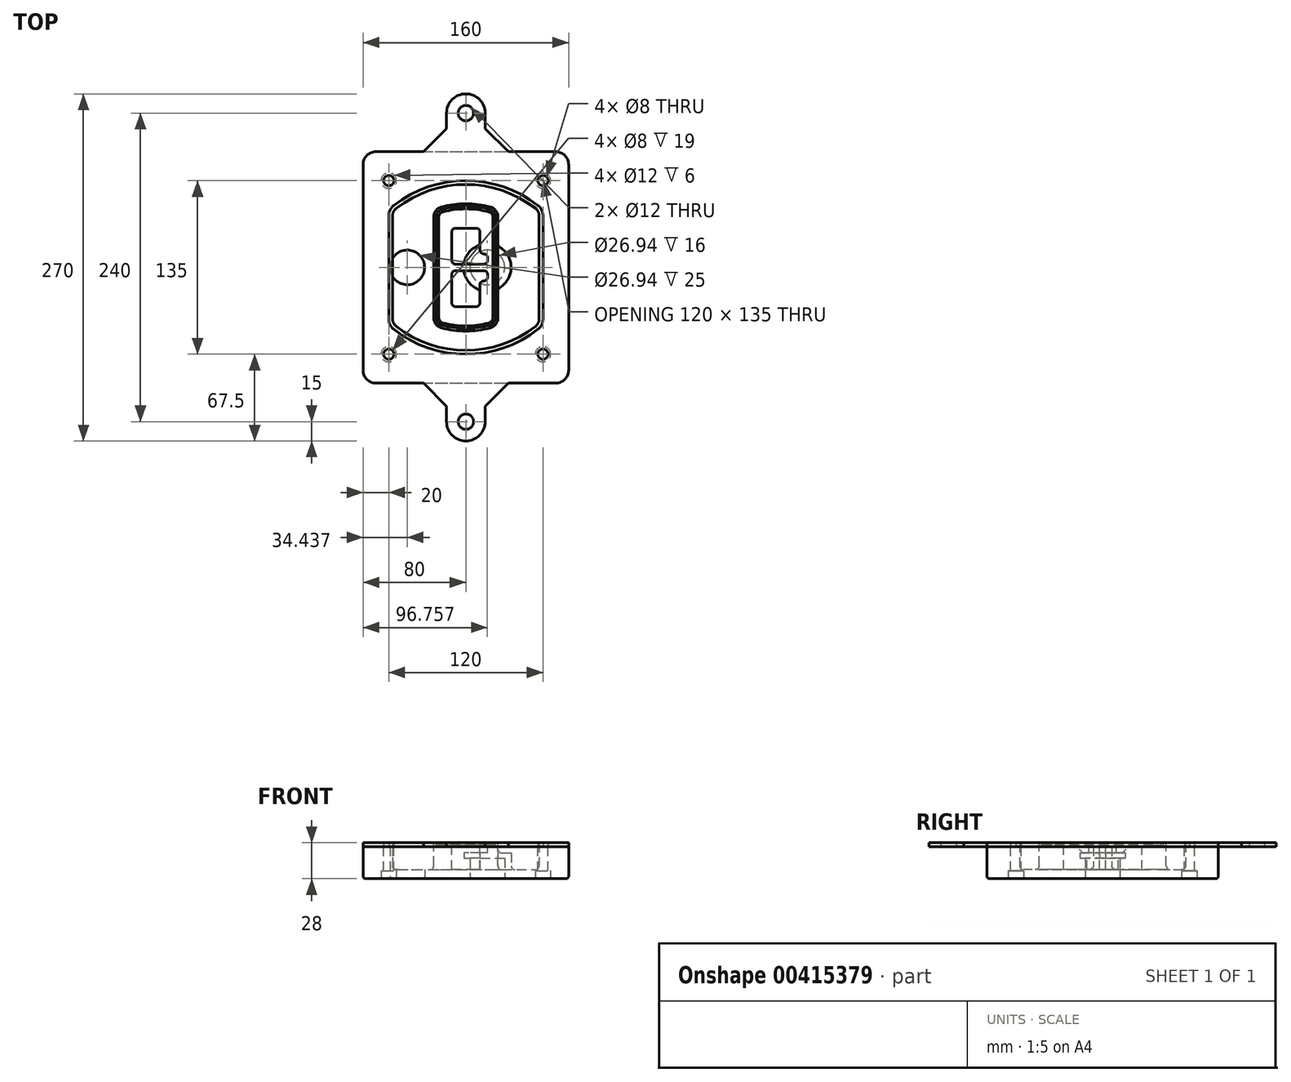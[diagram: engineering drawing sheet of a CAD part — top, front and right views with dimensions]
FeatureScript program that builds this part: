
annotation { "Feature Type Name" : "Feature", "Feature Type Description" : "" }
export const myFeature = defineFeature(function(context is Context, id is Id, definition is map)
    precondition{}
    {
        {
            var Q0;
            Q0=qCreatedBy(makeId("Top.planeOp"),FACE);
            var sketch = newSketch(context, id + "F0", { "sketchPlane" : qUnion([Q0])});
            skPoint(sketch, "E0.rect.middle", {"position": v(0, 0) * mm});
            skLineSegment(sketch, "E1.bottom", {"start": v(-70, -90) * mm, "end": v(70, -90) * mm});
            skLineSegment(sketch, "E1.top", {"start": v(-70, 90) * mm, "end": v(70, 90) * mm});
            skLineSegment(sketch, "E1.left", {"start": v(-80, -80) * mm, "end": v(-80, 80) * mm});
            skLineSegment(sketch, "E1.right", {"start": v(80, -80) * mm, "end": v(80, 80) * mm});
            skLineSegment(sketch, "E2", {"start": v(-80, 90) * mm, "end": v(80, -90) * mm, "construction": true});
            skLineSegment(sketch, "E3", {"start": v(80, 90) * mm, "end": v(-80, -90) * mm, "construction": true});
            skCircle(sketch, "E4", {"center": v(-60, 67.5) * mm, "radius": 4 * mm});
            skCircle(sketch, "E5", {"center": v(60, 67.5) * mm, "radius": 4 * mm});
            skCircle(sketch, "E6", {"center": v(60, -67.5) * mm, "radius": 4 * mm});
            skCircle(sketch, "E7", {"center": v(-60, -67.5) * mm, "radius": 4 * mm});
            skLineSegment(sketch, "E8", {"start": v(-60, 67.5) * mm, "end": v(60, 67.5) * mm, "construction": true});
            skLineSegment(sketch, "E9", {"start": v(60, 67.5) * mm, "end": v(60, -67.5) * mm, "construction": true});
            skLineSegment(sketch, "E10", {"start": v(60, -67.5) * mm, "end": v(-60, -67.5) * mm, "construction": true});
            skLineSegment(sketch, "E11", {"start": v(-60, -67.5) * mm, "end": v(-60, 67.5) * mm, "construction": true});
            skLineSegment(sketch, "E12", {"start": v(-60, 40.3) * mm, "end": v(-60, -40.3) * mm});
            skLineSegment(sketch, "E13", {"start": v(60, 40.3) * mm, "end": v(60, -40.3) * mm});
            skArc(sketch, "E14", {"start": v(56.15, 48.18) * mm, "mid": v(0, 67.5) * mm, "end": v(-56.15, 48.18) * mm});
            skArc(sketch, "E15", {"start": v(-56.15, -48.18) * mm, "mid": v(0, -67.5) * mm, "end": v(56.15, -48.18) * mm});
            skLineSegment(sketch, "E16", {"start": v(-60, 0) * mm, "end": v(60, 0) * mm, "construction": true});
            skPoint(sketch, "E17.visualSharp", {"position": v(-60, -45) * mm});
            skArc(sketch, "E17.filletArc", {"start": v(-60, -40.3) * mm, "mid": v(-58.99, -44.68) * mm, "end": v(-56.15, -48.18) * mm});
            skPoint(sketch, "E18.visualSharp", {"position": v(-60, 45) * mm});
            skArc(sketch, "E18.filletArc", {"start": v(-56.15, 48.18) * mm, "mid": v(-58.99, 44.68) * mm, "end": v(-60, 40.3) * mm});
            skPoint(sketch, "E19.visualSharp", {"position": v(60, 45) * mm});
            skArc(sketch, "E19.filletArc", {"start": v(60, 40.3) * mm, "mid": v(58.99, 44.68) * mm, "end": v(56.15, 48.18) * mm});
            skPoint(sketch, "E20.visualSharp", {"position": v(60, -45) * mm});
            skArc(sketch, "E20.filletArc", {"start": v(56.15, -48.18) * mm, "mid": v(58.99, -44.68) * mm, "end": v(60, -40.3) * mm});
            skPoint(sketch, "E21.visualSharp", {"position": v(-80, 90) * mm});
            skArc(sketch, "E21.filletArc", {"start": v(-70, 90) * mm, "mid": v(-77.07, 87.07) * mm, "end": v(-80, 80) * mm});
            skPoint(sketch, "E22.visualSharp", {"position": v(80, 90) * mm});
            skArc(sketch, "E22.filletArc", {"start": v(80, 80) * mm, "mid": v(77.07, 87.07) * mm, "end": v(70, 90) * mm});
            skPoint(sketch, "E23.visualSharp", {"position": v(80, -90) * mm});
            skArc(sketch, "E23.filletArc", {"start": v(70, -90) * mm, "mid": v(77.07, -87.07) * mm, "end": v(80, -80) * mm});
            skPoint(sketch, "E24.visualSharp", {"position": v(-80, -90) * mm});
            skArc(sketch, "E24.filletArc", {"start": v(-80, -80) * mm, "mid": v(-77.07, -87.07) * mm, "end": v(-70, -90) * mm});
            skArc(sketch, "E25.0", {"start": v(57, 40.3) * mm, "mid": v(56.3, 43.36) * mm, "end": v(54.3, 45.81) * mm});
            skLineSegment(sketch, "E25.1", {"start": v(57, 40.3) * mm, "end": v(57, -40.3) * mm});
            skArc(sketch, "E25.2", {"start": v(54.3, -45.81) * mm, "mid": v(56.3, -43.36) * mm, "end": v(57, -40.3) * mm});
            skArc(sketch, "E25.3", {"start": v(-54.3, -45.81) * mm, "mid": v(0, -64.5) * mm, "end": v(54.3, -45.81) * mm});
            skArc(sketch, "E25.4", {"start": v(-57, -40.3) * mm, "mid": v(-56.3, -43.36) * mm, "end": v(-54.3, -45.81) * mm});
            skArc(sketch, "E25.5", {"start": v(54.3, 45.81) * mm, "mid": v(0, 64.5) * mm, "end": v(-54.3, 45.81) * mm});
            skLineSegment(sketch, "E25.6", {"start": v(-57, 40.3) * mm, "end": v(-57, -40.3) * mm});
            skArc(sketch, "E25.7", {"start": v(-54.3, 45.81) * mm, "mid": v(-56.3, 43.36) * mm, "end": v(-57, 40.3) * mm});
            skArc(sketch, "E26.0", {"start": v(-58.62, 51.33) * mm, "mid": v(-62.58, 46.43) * mm, "end": v(-64, 40.3) * mm});
            skArc(sketch, "E26.1", {"start": v(58.62, 51.33) * mm, "mid": v(0, 71.5) * mm, "end": v(-58.62, 51.33) * mm});
            skArc(sketch, "E26.2", {"start": v(64, 40.3) * mm, "mid": v(62.58, 46.43) * mm, "end": v(58.62, 51.33) * mm});
            skLineSegment(sketch, "E26.3", {"start": v(64, 40.3) * mm, "end": v(64, -40.3) * mm});
            skArc(sketch, "E26.4", {"start": v(58.62, -51.33) * mm, "mid": v(62.58, -46.43) * mm, "end": v(64, -40.3) * mm});
            skLineSegment(sketch, "E26.5", {"start": v(-64, 40.3) * mm, "end": v(-64, -40.3) * mm});
            skArc(sketch, "E26.6", {"start": v(-58.62, -51.33) * mm, "mid": v(0, -71.5) * mm, "end": v(58.62, -51.33) * mm});
            skArc(sketch, "E26.7", {"start": v(-64, -40.3) * mm, "mid": v(-62.58, -46.43) * mm, "end": v(-58.62, -51.33) * mm});
            skSolve(sketch);
        }
        {
            var Q0;
            Q0=makeQuery(id+"F0.imprint","IMPRINT",FACE,{"disambiguationData":[TD([[makeQuery(id+"F0.imprint","IMPRINT",EDGE,{"derivedFrom":sQuery(id+"F0.wireOp",EDGE,"E1.bottom")}),1.0]])]});
            var Q1;
            Q1=makeQuery(id+"F0.imprint","IMPRINT",FACE,{"disambiguationData":[TD([[makeQuery(id+"F0.imprint","IMPRINT",EDGE,{"derivedFrom":sQuery(id+"F0.wireOp",EDGE,"E12")}),1.0]])]});
            var Q2;
            Q2=makeQuery(id+"F0.imprint","IMPRINT",FACE,{"disambiguationData":[TD([[makeQuery(id+"F0.imprint","IMPRINT",EDGE,{"derivedFrom":sQuery(id+"F0.wireOp",EDGE,"E25.0")}),1.0]])]});
            var Q3;
            Q3=makeQuery(id+"F0.imprint","IMPRINT",FACE,{"disambiguationData":[TD([[makeQuery(id+"F0.imprint","IMPRINT",EDGE,{"derivedFrom":sQuery(id+"F0.wireOp",EDGE,"E12")}),-1.0]])]});
            extrude(context, id + "F1", {"entities" : qUnion([Q0, Q1, Q2, Q3]), "oppositeDirection" : true, "depth" : 25 * mm});
        }
        {
            var Q0;
            Q0=makeQuery(id+"F0.imprint","IMPRINT",FACE,{"disambiguationData":[TD([[makeQuery(id+"F0.imprint","IMPRINT",EDGE,{"derivedFrom":sQuery(id+"F0.wireOp",EDGE,"E12")}),1.0]])]});
            extrude(context, id + "F2", {"entities" : qUnion([Q0]), "operationType" : NewBodyOperationType.ADD, "depth" : 3 * mm});
        }
        {
            var Q0;
            Q0=makeQuery(id+"F0.imprint","IMPRINT",FACE,{"disambiguationData":[TD([[makeQuery(id+"F0.imprint","IMPRINT",EDGE,{"derivedFrom":sQuery(id+"F0.wireOp",EDGE,"E25.0")}),1.0]])]});
            extrude(context, id + "F3", {"entities" : qUnion([Q0]), "operationType" : NewBodyOperationType.REMOVE, "oppositeDirection" : true, "depth" : 18 * mm});
        }
        {
            var Q0;
            Q0=makeQuery(id+"F2.opExtrude","CAP_FACE",FACE,{"disambiguationData":[OSD([sQuery(id+"F0.wireOp",EDGE,"E12"),sQuery(id+"F0.wireOp",EDGE,"E13"),sQuery(id+"F0.wireOp",EDGE,"E14"),sQuery(id+"F0.wireOp",EDGE,"E15"),sQuery(id+"F0.wireOp",EDGE,"E17.filletArc"),sQuery(id+"F0.wireOp",EDGE,"E18.filletArc"),sQuery(id+"F0.wireOp",EDGE,"E19.filletArc"),sQuery(id+"F0.wireOp",EDGE,"E20.filletArc"),sQuery(id+"F0.wireOp",EDGE,"E25.0"),sQuery(id+"F0.wireOp",EDGE,"E25.1"),sQuery(id+"F0.wireOp",EDGE,"E25.2"),sQuery(id+"F0.wireOp",EDGE,"E25.3"),sQuery(id+"F0.wireOp",EDGE,"E25.4"),sQuery(id+"F0.wireOp",EDGE,"E25.5"),sQuery(id+"F0.wireOp",EDGE,"E25.6"),sQuery(id+"F0.wireOp",EDGE,"E25.7")])],"isStart":false});
            var sketch = newSketch(context, id + "F4", { "sketchPlane" : qUnion([Q0])});
            skArc(sketch, "E27.0", {"start": v(-19.08, -46.97) * mm, "mid": v(0, -49.5) * mm, "end": v(19.08, -46.97) * mm});
            skArc(sketch, "E28.0", {"start": v(19.08, 46.97) * mm, "mid": v(0, 49.5) * mm, "end": v(-19.08, 46.97) * mm});
            skLineSegment(sketch, "E29", {"start": v(-25, 39.25) * mm, "end": v(-25, -39.25) * mm});
            skLineSegment(sketch, "E30", {"start": v(25, 39.25) * mm, "end": v(25, -39.25) * mm});
            skLineSegment(sketch, "E31", {"start": v(-25, 45.1) * mm, "end": v(25, 45.1) * mm, "construction": true});
            skLineSegment(sketch, "E32", {"start": v(-25, -45.1) * mm, "end": v(25, -45.1) * mm, "construction": true});
            skPoint(sketch, "E33.visualSharp", {"position": v(-25, 45.1) * mm});
            skArc(sketch, "E33.filletArc", {"start": v(-19.08, 46.97) * mm, "mid": v(-23.35, 44.11) * mm, "end": v(-25, 39.25) * mm});
            skPoint(sketch, "E34.visualSharp", {"position": v(25, 45.1) * mm});
            skArc(sketch, "E34.filletArc", {"start": v(25, 39.25) * mm, "mid": v(23.35, 44.11) * mm, "end": v(19.08, 46.97) * mm});
            skPoint(sketch, "E35.visualSharp", {"position": v(25, -45.1) * mm});
            skArc(sketch, "E35.filletArc", {"start": v(19.08, -46.97) * mm, "mid": v(23.35, -44.11) * mm, "end": v(25, -39.25) * mm});
            skPoint(sketch, "E36.visualSharp", {"position": v(-25, -45.1) * mm});
            skArc(sketch, "E36.filletArc", {"start": v(-25, -39.25) * mm, "mid": v(-23.35, -44.11) * mm, "end": v(-19.08, -46.97) * mm});
            skArc(sketch, "E37.0", {"start": v(54.3, 45.81) * mm, "mid": v(0, 64.5) * mm, "end": v(-54.3, 45.81) * mm});
            skArc(sketch, "E37.1", {"start": v(-54.3, 45.81) * mm, "mid": v(-56.3, 43.36) * mm, "end": v(-57, 40.3) * mm});
            skLineSegment(sketch, "E37.2", {"start": v(-57, 40.3) * mm, "end": v(-57, -40.3) * mm});
            skArc(sketch, "E37.3", {"start": v(-57, -40.3) * mm, "mid": v(-56.3, -43.36) * mm, "end": v(-54.3, -45.81) * mm});
            skArc(sketch, "E37.4", {"start": v(-54.3, -45.81) * mm, "mid": v(0, -64.5) * mm, "end": v(54.3, -45.81) * mm});
            skArc(sketch, "E37.5", {"start": v(54.3, -45.81) * mm, "mid": v(56.3, -43.36) * mm, "end": v(57, -40.3) * mm});
            skLineSegment(sketch, "E37.6", {"start": v(57, 40.3) * mm, "end": v(57, -40.3) * mm});
            skArc(sketch, "E37.7", {"start": v(57, 40.3) * mm, "mid": v(56.3, 43.36) * mm, "end": v(54.3, 45.81) * mm});
            skLineSegment(sketch, "E38.0", {"start": v(23, 39.25) * mm, "end": v(23, -39.25) * mm});
            skArc(sketch, "E38.1", {"start": v(18.56, -45.04) * mm, "mid": v(21.76, -42.9) * mm, "end": v(23, -39.25) * mm});
            skArc(sketch, "E38.2", {"start": v(-18.56, -45.04) * mm, "mid": v(0, -47.5) * mm, "end": v(18.56, -45.04) * mm});
            skArc(sketch, "E38.3", {"start": v(-23, -39.25) * mm, "mid": v(-21.76, -42.9) * mm, "end": v(-18.56, -45.04) * mm});
            skLineSegment(sketch, "E38.4", {"start": v(-23, 39.25) * mm, "end": v(-23, -39.25) * mm});
            skArc(sketch, "E38.5", {"start": v(23, 39.25) * mm, "mid": v(21.76, 42.9) * mm, "end": v(18.56, 45.04) * mm});
            skArc(sketch, "E38.6", {"start": v(-18.56, 45.04) * mm, "mid": v(-21.76, 42.9) * mm, "end": v(-23, 39.25) * mm});
            skArc(sketch, "E38.7", {"start": v(18.56, 45.04) * mm, "mid": v(0, 47.5) * mm, "end": v(-18.56, 45.04) * mm});
            skArc(sketch, "E39.0", {"start": v(21, 39.25) * mm, "mid": v(20.18, 41.68) * mm, "end": v(18.04, 43.1) * mm});
            skLineSegment(sketch, "E39.1", {"start": v(21, 39.25) * mm, "end": v(21, -39.25) * mm});
            skArc(sketch, "E39.2", {"start": v(18.04, -43.1) * mm, "mid": v(20.18, -41.68) * mm, "end": v(21, -39.25) * mm});
            skArc(sketch, "E39.3", {"start": v(-18.04, -43.1) * mm, "mid": v(0, -45.5) * mm, "end": v(18.04, -43.1) * mm});
            skArc(sketch, "E39.4", {"start": v(-21, -39.25) * mm, "mid": v(-20.18, -41.68) * mm, "end": v(-18.04, -43.1) * mm});
            skArc(sketch, "E39.5", {"start": v(18.04, 43.1) * mm, "mid": v(0, 45.5) * mm, "end": v(-18.04, 43.1) * mm});
            skLineSegment(sketch, "E39.6", {"start": v(-21, 39.25) * mm, "end": v(-21, -39.25) * mm});
            skArc(sketch, "E39.7", {"start": v(-18.04, 43.1) * mm, "mid": v(-20.18, 41.68) * mm, "end": v(-21, 39.25) * mm});
            skLineSegment(sketch, "E40", {"start": v(-25, 0) * mm, "end": v(25, 0) * mm, "construction": true});
            skLineSegment(sketch, "E41", {"start": v(-11, 5.5) * mm, "end": v(-11, 27.5) * mm});
            skLineSegment(sketch, "E42", {"start": v(-8, 30.5) * mm, "end": v(8, 30.5) * mm});
            skLineSegment(sketch, "E43", {"start": v(11, 27.5) * mm, "end": v(11, 13.5) * mm});
            skLineSegment(sketch, "E44", {"start": v(14, 10.5) * mm, "end": v(14, 10.5) * mm});
            skLineSegment(sketch, "E45", {"start": v(17, 7.5) * mm, "end": v(17, 5.5) * mm});
            skLineSegment(sketch, "E46", {"start": v(14, 2.5) * mm, "end": v(-8, 2.5) * mm});
            skPoint(sketch, "E47.visualSharp", {"position": v(-11, 30.5) * mm});
            skArc(sketch, "E47.filletArc", {"start": v(-8, 30.5) * mm, "mid": v(-10.12, 29.62) * mm, "end": v(-11, 27.5) * mm});
            skPoint(sketch, "E48.visualSharp", {"position": v(11, 30.5) * mm});
            skArc(sketch, "E48.filletArc", {"start": v(11, 27.5) * mm, "mid": v(10.12, 29.62) * mm, "end": v(8, 30.5) * mm});
            skPoint(sketch, "E49.visualSharp", {"position": v(11, 10.5) * mm});
            skArc(sketch, "E49.filletArc", {"start": v(11, 13.5) * mm, "mid": v(11.88, 11.38) * mm, "end": v(14, 10.5) * mm});
            skPoint(sketch, "E50.visualSharp", {"position": v(17, 10.5) * mm});
            skArc(sketch, "E50.filletArc", {"start": v(17, 7.5) * mm, "mid": v(16.12, 9.62) * mm, "end": v(14, 10.5) * mm});
            skPoint(sketch, "E51.visualSharp", {"position": v(17, 2.5) * mm});
            skArc(sketch, "E51.filletArc", {"start": v(14, 2.5) * mm, "mid": v(16.12, 3.38) * mm, "end": v(17, 5.5) * mm});
            skPoint(sketch, "E52.visualSharp", {"position": v(-11, 2.5) * mm});
            skArc(sketch, "E52.filletArc", {"start": v(-11, 5.5) * mm, "mid": v(-10.12, 3.38) * mm, "end": v(-8, 2.5) * mm});
            skLineSegment(sketch, "E53.0.MirrorCS", {"start": v(14, -2.5) * mm, "end": v(-8, -2.5) * mm});
            skArc(sketch, "E54.0.MirrorCS", {"start": v(-11, -5.5) * mm, "mid": v(-10.12, -3.38) * mm, "end": v(-8, -2.5) * mm});
            skLineSegment(sketch, "E55.0.MirrorCS", {"start": v(-11, -5.5) * mm, "end": v(-11, -27.5) * mm});
            skArc(sketch, "E56.0.MirrorCS", {"start": v(-8, -30.5) * mm, "mid": v(-10.12, -29.62) * mm, "end": v(-11, -27.5) * mm});
            skLineSegment(sketch, "E57.0.MirrorCS", {"start": v(-8, -30.5) * mm, "end": v(8, -30.5) * mm});
            skArc(sketch, "E58.0.MirrorCS", {"start": v(11, -27.5) * mm, "mid": v(10.12, -29.62) * mm, "end": v(8, -30.5) * mm});
            skLineSegment(sketch, "E59.0.MirrorCS", {"start": v(11, -27.5) * mm, "end": v(11, -13.5) * mm});
            skArc(sketch, "E60.0.MirrorCS", {"start": v(11, -13.5) * mm, "mid": v(11.88, -11.38) * mm, "end": v(14, -10.5) * mm});
            skArc(sketch, "E61.0.MirrorCS", {"start": v(17, -7.5) * mm, "mid": v(16.12, -9.62) * mm, "end": v(14, -10.5) * mm});
            skLineSegment(sketch, "E62.0.MirrorCS", {"start": v(17, -7.5) * mm, "end": v(17, -5.5) * mm});
            skArc(sketch, "E63.0.MirrorCS", {"start": v(14, -2.5) * mm, "mid": v(16.12, -3.38) * mm, "end": v(17, -5.5) * mm});
            skSolve(sketch);
        }
        {
            var Q0;
            Q0=makeQuery(id+"F4.imprint","IMPRINT",FACE,{"disambiguationData":[TD([[makeQuery(id+"F4.imprint","IMPRINT",EDGE,{"derivedFrom":sQuery(id+"F4.wireOp",EDGE,"E27.0")}),1.0]])]});
            var Q1;
            Q1=makeQuery(id+"F4.imprint","IMPRINT",FACE,{"disambiguationData":[TD([[makeQuery(id+"F4.imprint","IMPRINT",EDGE,{"derivedFrom":sQuery(id+"F4.wireOp",EDGE,"E38.0")}),-1.0]])]});
            var Q2;
            Q2=makeQuery(id+"F4.imprint","IMPRINT",FACE,{"disambiguationData":[TD([[makeQuery(id+"F4.imprint","IMPRINT",EDGE,{"derivedFrom":sQuery(id+"F4.wireOp",EDGE,"E39.0")}),1.0]])]});
            extrude(context, id + "F5", {"entities" : qUnion([Q0, Q1, Q2]), "operationType" : NewBodyOperationType.ADD, "endBound" : BoundingType.UP_TO_NEXT, "oppositeDirection" : true, "depth" : 25 * mm});
        }
        {
            var Q0;
            Q0=makeQuery(id+"F4.imprint","IMPRINT",FACE,{"disambiguationData":[TD([[makeQuery(id+"F4.imprint","IMPRINT",EDGE,{"derivedFrom":sQuery(id+"F4.wireOp",EDGE,"E38.0")}),-1.0]])]});
            extrude(context, id + "F6", {"entities" : qUnion([Q0]), "operationType" : NewBodyOperationType.REMOVE, "oppositeDirection" : true, "depth" : 2 * mm});
        }
        {
            var Q0;
            Q0=makeQuery(id+"F1.opExtrude","CAP_FACE",FACE,{"disambiguationData":[OSD([sQuery(id+"F0.wireOp",EDGE,"E1.bottom"),sQuery(id+"F0.wireOp",EDGE,"E1.top"),sQuery(id+"F0.wireOp",EDGE,"E1.left"),sQuery(id+"F0.wireOp",EDGE,"E1.right"),sQuery(id+"F0.wireOp",EDGE,"E4"),sQuery(id+"F0.wireOp",EDGE,"E5"),sQuery(id+"F0.wireOp",EDGE,"E6"),sQuery(id+"F0.wireOp",EDGE,"E7"),sQuery(id+"F0.wireOp",EDGE,"E21.filletArc"),sQuery(id+"F0.wireOp",EDGE,"E22.filletArc"),sQuery(id+"F0.wireOp",EDGE,"E23.filletArc"),sQuery(id+"F0.wireOp",EDGE,"E24.filletArc")])],"isStart":false});
            var sketch = newSketch(context, id + "F7", { "sketchPlane" : qUnion([Q0])});
            skCircle(sketch, "E64", {"center": v(16.76, 0) * mm, "radius": 13.47 * mm});
            skCircle(sketch, "E65", {"center": v(-45.56, 0) * mm, "radius": 13.47 * mm});
            skLineSegment(sketch, "E66", {"start": v(80, 0) * mm, "end": v(-80, 0) * mm});
            skCircle(sketch, "E67", {"center": v(16.76, 0) * mm, "radius": 18.47 * mm});
            skCircle(sketch, "E68", {"center": v(60, -67.5) * mm, "radius": 6 * mm});
            skCircle(sketch, "E69", {"center": v(-60, -67.5) * mm, "radius": 6 * mm});
            skCircle(sketch, "E70", {"center": v(-60, 67.5) * mm, "radius": 6 * mm});
            skCircle(sketch, "E71", {"center": v(60, 67.5) * mm, "radius": 6 * mm});
            skSolve(sketch);
        }
        {
            var Q0;
            {var subQ1=sQuery(id+"F7.wireOp",EDGE,"E66");var subQ4=sQuery(id+"F7.wireOp",EDGE,"E64");var subQ6=makeQuery(id+"F7.imprint","INTERSECT",VERTEX,{"disambiguationData":[OD(0.0)],"derivedFrom":[subQ4,subQ1]});Q0=makeQuery(id+"F7.imprint","IMPRINT",FACE,{"disambiguationData":[TD([[makeQuery(id+"F7.imprint","IMPRINT",EDGE,{"disambiguationData":[TD([[subQ6,-1.0]])],"derivedFrom":subQ4}),-1.0]])]});}
            var Q1;
            {var subQ0=sQuery(id+"F7.wireOp",EDGE,"E66");var subQ1=sQuery(id+"F7.wireOp",EDGE,"E64");var subQ3=makeQuery(id+"F7.imprint","INTERSECT",VERTEX,{"disambiguationData":[OD(0.0)],"derivedFrom":[subQ1,subQ0]});Q1=makeQuery(id+"F7.imprint","IMPRINT",FACE,{"disambiguationData":[TD([[makeQuery(id+"F7.imprint","IMPRINT",EDGE,{"disambiguationData":[TD([[subQ3,-1.0]])],"derivedFrom":subQ1}),1.0]])]});}
            var Q2;
            {var subQ0=sQuery(id+"F7.wireOp",EDGE,"E66");var subQ1=sQuery(id+"F7.wireOp",EDGE,"E64");var subQ3=makeQuery(id+"F7.imprint","INTERSECT",VERTEX,{"disambiguationData":[OD(0.0)],"derivedFrom":[subQ1,subQ0]});Q2=makeQuery(id+"F7.imprint","IMPRINT",FACE,{"disambiguationData":[TD([[makeQuery(id+"F7.imprint","IMPRINT",EDGE,{"disambiguationData":[TD([[subQ3,1.0]])],"derivedFrom":subQ1}),1.0]])]});}
            var Q3;
            {var subQ1=sQuery(id+"F7.wireOp",EDGE,"E66");var subQ4=sQuery(id+"F7.wireOp",EDGE,"E64");var subQ6=makeQuery(id+"F7.imprint","INTERSECT",VERTEX,{"disambiguationData":[OD(0.0)],"derivedFrom":[subQ4,subQ1]});Q3=makeQuery(id+"F7.imprint","IMPRINT",FACE,{"disambiguationData":[TD([[makeQuery(id+"F7.imprint","IMPRINT",EDGE,{"disambiguationData":[TD([[subQ6,1.0]])],"derivedFrom":subQ4}),-1.0]])]});}
            extrude(context, id + "F8", {"entities" : qUnion([Q0, Q1, Q2, Q3]), "operationType" : NewBodyOperationType.ADD, "oppositeDirection" : true, "depth" : 20 * mm});
        }
        {
            var Q0;
            {var subQ0=sQuery(id+"F7.wireOp",EDGE,"E66");var subQ1=sQuery(id+"F7.wireOp",EDGE,"E64");var subQ3=makeQuery(id+"F7.imprint","INTERSECT",VERTEX,{"disambiguationData":[OD(0.0)],"derivedFrom":[subQ1,subQ0]});Q0=makeQuery(id+"F7.imprint","IMPRINT",FACE,{"disambiguationData":[TD([[makeQuery(id+"F7.imprint","IMPRINT",EDGE,{"disambiguationData":[TD([[subQ3,-1.0]])],"derivedFrom":subQ1}),1.0]])]});}
            var Q1;
            {var subQ0=sQuery(id+"F7.wireOp",EDGE,"E66");var subQ1=sQuery(id+"F7.wireOp",EDGE,"E64");var subQ3=makeQuery(id+"F7.imprint","INTERSECT",VERTEX,{"disambiguationData":[OD(0.0)],"derivedFrom":[subQ1,subQ0]});Q1=makeQuery(id+"F7.imprint","IMPRINT",FACE,{"disambiguationData":[TD([[makeQuery(id+"F7.imprint","IMPRINT",EDGE,{"disambiguationData":[TD([[subQ3,1.0]])],"derivedFrom":subQ1}),1.0]])]});}
            extrude(context, id + "F9", {"entities" : qUnion([Q0, Q1]), "operationType" : NewBodyOperationType.REMOVE, "oppositeDirection" : true, "depth" : 16 * mm});
        }
        {
            var Q0;
            {var subQ0=sQuery(id+"F7.wireOp",EDGE,"E66");var subQ1=sQuery(id+"F7.wireOp",EDGE,"E65");var subQ3=makeQuery(id+"F7.imprint","INTERSECT",VERTEX,{"disambiguationData":[OD(0.0)],"derivedFrom":[subQ1,subQ0]});Q0=makeQuery(id+"F7.imprint","IMPRINT",FACE,{"disambiguationData":[TD([[makeQuery(id+"F7.imprint","IMPRINT",EDGE,{"disambiguationData":[TD([[subQ3,-1.0]])],"derivedFrom":subQ1}),1.0]])]});}
            var Q1;
            {var subQ0=sQuery(id+"F7.wireOp",EDGE,"E66");var subQ1=sQuery(id+"F7.wireOp",EDGE,"E65");var subQ3=makeQuery(id+"F7.imprint","INTERSECT",VERTEX,{"disambiguationData":[OD(0.0)],"derivedFrom":[subQ1,subQ0]});Q1=makeQuery(id+"F7.imprint","IMPRINT",FACE,{"disambiguationData":[TD([[makeQuery(id+"F7.imprint","IMPRINT",EDGE,{"disambiguationData":[TD([[subQ3,1.0]])],"derivedFrom":subQ1}),1.0]])]});}
            extrude(context, id + "F10", {"entities" : qUnion([Q0, Q1]), "operationType" : NewBodyOperationType.REMOVE, "oppositeDirection" : true, "depth" : 25 * mm});
        }
        {
            var Q0;
            Q0=makeQuery(id+"F7.imprint","IMPRINT",FACE,{"disambiguationData":[TD([[makeQuery(id+"F7.imprint","IMPRINT",EDGE,{"derivedFrom":sQuery(id+"F7.wireOp",EDGE,"E68")}),1.0]])]});
            var Q1;
            Q1=makeQuery(id+"F7.imprint","IMPRINT",FACE,{"disambiguationData":[TD([[makeQuery(id+"F7.imprint","IMPRINT",EDGE,{"derivedFrom":makeQuery(id+"F1.opExtrude","CAP_EDGE",EDGE,{"disambiguationData":[OSD([sQuery(id+"F0.wireOp",EDGE,"E5")])],"isStart":false})}),-1.0]])]});
            var Q2;
            Q2=makeQuery(id+"F7.imprint","IMPRINT",FACE,{"disambiguationData":[TD([[makeQuery(id+"F7.imprint","IMPRINT",EDGE,{"derivedFrom":sQuery(id+"F7.wireOp",EDGE,"E69")}),1.0]])]});
            var Q3;
            Q3=makeQuery(id+"F7.imprint","IMPRINT",FACE,{"disambiguationData":[TD([[makeQuery(id+"F7.imprint","IMPRINT",EDGE,{"derivedFrom":makeQuery(id+"F1.opExtrude","CAP_EDGE",EDGE,{"disambiguationData":[OSD([sQuery(id+"F0.wireOp",EDGE,"E4")])],"isStart":false})}),-1.0]])]});
            var Q4;
            Q4=makeQuery(id+"F7.imprint","IMPRINT",FACE,{"disambiguationData":[TD([[makeQuery(id+"F7.imprint","IMPRINT",EDGE,{"derivedFrom":sQuery(id+"F7.wireOp",EDGE,"E70")}),1.0]])]});
            var Q5;
            Q5=makeQuery(id+"F7.imprint","IMPRINT",FACE,{"disambiguationData":[TD([[makeQuery(id+"F7.imprint","IMPRINT",EDGE,{"derivedFrom":makeQuery(id+"F1.opExtrude","CAP_EDGE",EDGE,{"disambiguationData":[OSD([sQuery(id+"F0.wireOp",EDGE,"E7")])],"isStart":false})}),-1.0]])]});
            var Q6;
            Q6=makeQuery(id+"F7.imprint","IMPRINT",FACE,{"disambiguationData":[TD([[makeQuery(id+"F7.imprint","IMPRINT",EDGE,{"derivedFrom":sQuery(id+"F7.wireOp",EDGE,"E71")}),1.0]])]});
            var Q7;
            Q7=makeQuery(id+"F7.imprint","IMPRINT",FACE,{"disambiguationData":[TD([[makeQuery(id+"F7.imprint","IMPRINT",EDGE,{"derivedFrom":makeQuery(id+"F1.opExtrude","CAP_EDGE",EDGE,{"disambiguationData":[OSD([sQuery(id+"F0.wireOp",EDGE,"E6")])],"isStart":false})}),-1.0]])]});
            extrude(context, id + "F11", {"entities" : qUnion([Q0, Q1, Q2, Q3, Q4, Q5, Q6, Q7]), "operationType" : NewBodyOperationType.REMOVE, "oppositeDirection" : true, "depth" : 6 * mm});
        }
        {
            var Q0;
            Q0=makeQuery(id+"F9.boolean.opBoolean","COPY",FACE,{"derivedFrom":makeQuery(id+"F9.opExtrude","CAP_FACE",FACE,{"disambiguationData":[OSD([sQuery(id+"F7.wireOp",EDGE,"E64")])],"isStart":false})});
            var sketch = newSketch(context, id + "F12", { "sketchPlane" : qUnion([Q0])});
            skArc(sketch, "E72.0", {"start": v(11, 17.55) * mm, "mid": v(2.57, 11.82) * mm, "end": v(-1.54, 2.5) * mm});
            skArc(sketch, "E72.1", {"start": v(-1.54, -2.5) * mm, "mid": v(2.57, -11.82) * mm, "end": v(11, -17.55) * mm});
            skLineSegment(sketch, "E73", {"start": v(-1.54, -2.5) * mm, "end": v(14, -2.5) * mm});
            skLineSegment(sketch, "E74.0", {"start": v(14, 2.5) * mm, "end": v(-1.54, 2.5) * mm});
            skArc(sketch, "E74.1", {"start": v(14, 2.5) * mm, "mid": v(16.12, 3.38) * mm, "end": v(17, 5.5) * mm});
            skLineSegment(sketch, "E74.2", {"start": v(17, 7.5) * mm, "end": v(17, 5.5) * mm});
            skArc(sketch, "E74.3", {"start": v(17, 7.5) * mm, "mid": v(16.12, 9.62) * mm, "end": v(14, 10.5) * mm});
            skArc(sketch, "E74.4", {"start": v(11, 13.5) * mm, "mid": v(11.88, 11.38) * mm, "end": v(14, 10.5) * mm});
            skLineSegment(sketch, "E74.5", {"start": v(11, 17.55) * mm, "end": v(11, 13.5) * mm});
            skLineSegment(sketch, "E74.7", {"start": v(14, -2.5) * mm, "end": v(-1.54, -2.5) * mm});
            skArc(sketch, "E74.8", {"start": v(14, -2.5) * mm, "mid": v(16.12, -3.38) * mm, "end": v(17, -5.5) * mm});
            skLineSegment(sketch, "E74.9", {"start": v(17, -7.5) * mm, "end": v(17, -5.5) * mm});
            skArc(sketch, "E74.10", {"start": v(17, -7.5) * mm, "mid": v(16.12, -9.62) * mm, "end": v(14, -10.5) * mm});
            skArc(sketch, "E74.11", {"start": v(11, -13.5) * mm, "mid": v(11.88, -11.38) * mm, "end": v(14, -10.5) * mm});
            skLineSegment(sketch, "E74.12", {"start": v(11, -17.55) * mm, "end": v(11, -13.5) * mm});
            skPoint(sketch, "E75.orphan", {"position": v(11, -27.5) * mm});
            skPoint(sketch, "E76.orphan", {"position": v(-8, -2.5) * mm});
            skPoint(sketch, "E77.orphan", {"position": v(-8, 2.5) * mm});
            skPoint(sketch, "E78.orphan", {"position": v(11, 27.5) * mm});
            skSolve(sketch);
        }
        {
            var Q0;
            {var subQ7=sQuery(id+"F12.wireOp",EDGE,"E72.0");var subQ14=sQuery(id+"F12.wireOp",EDGE,"E72.1");var subQ16=sQuery(id+"F12.wireOp",EDGE,"E74.1");var subQ18=sQuery(id+"F12.wireOp",EDGE,"E74.8");Q0=qUnion([makeQuery(id+"F12.imprint","IMPRINT",FACE,{"disambiguationData":[TD([[makeQuery(id+"F12.imprint","IMPRINT",EDGE,{"derivedFrom":subQ7}),1.0]])]}),makeQuery(id+"F12.imprint","IMPRINT",FACE,{"disambiguationData":[TD([[makeQuery(id+"F12.imprint","IMPRINT",EDGE,{"derivedFrom":subQ14}),1.0]])]}),makeQuery(id+"F12.imprint","IMPRINT",FACE,{"disambiguationData":[TD([[makeQuery(id+"F12.imprint","IMPRINT",EDGE,{"derivedFrom":subQ16}),1.0]])]}),makeQuery(id+"F12.imprint","IMPRINT",FACE,{"disambiguationData":[TD([[makeQuery(id+"F12.imprint","IMPRINT",EDGE,{"derivedFrom":subQ18}),-1.0]])]})]);}
            var Q1;
            Q1=makeQuery(id+"F5.boolean.opBoolean","SPLIT",FACE,{"disambiguationData":[TD([makeQuery(id+"F5.opExtrude","SWEPT_FACE",FACE,{"disambiguationData":[OSD([sQuery(id+"F4.wireOp",EDGE,"E41")])]})])],"derivedFrom":makeQuery(id+"F3.boolean.opBoolean","COPY",FACE,{"derivedFrom":makeQuery(id+"F3.opExtrude","CAP_FACE",FACE,{"disambiguationData":[OSD([sQuery(id+"F0.wireOp",EDGE,"E25.0"),sQuery(id+"F0.wireOp",EDGE,"E25.1"),sQuery(id+"F0.wireOp",EDGE,"E25.2"),sQuery(id+"F0.wireOp",EDGE,"E25.3"),sQuery(id+"F0.wireOp",EDGE,"E25.4"),sQuery(id+"F0.wireOp",EDGE,"E25.5"),sQuery(id+"F0.wireOp",EDGE,"E25.6"),sQuery(id+"F0.wireOp",EDGE,"E25.7")])],"isStart":false})})});
            extrude(context, id + "F13", {"entities" : qUnion([Q0]), "operationType" : NewBodyOperationType.REMOVE, "endBound" : BoundingType.UP_TO_SURFACE, "endBoundEntityFace" : qUnion([Q1]), "depth" : 25 * mm});
        }
        {
            var Q0;
            Q0=makeQuery(id+"F3.boolean.opBoolean","COPY",EDGE,{"derivedFrom":makeQuery(id+"F3.opExtrude","CAP_EDGE",EDGE,{"disambiguationData":[OSD([sQuery(id+"F0.wireOp",EDGE,"E25.6")])],"isStart":false})});
            var Q1;
            Q1=makeQuery(id+"F8.boolean.opBoolean","INTERSECT",EDGE,{"derivedFrom":[makeQuery(id+"F5.opExtrude","SWEPT_FACE",FACE,{"disambiguationData":[OSD([sQuery(id+"F4.wireOp",EDGE,"E30")])]}),makeQuery(id+"F8.opExtrude","CAP_FACE",FACE,{"disambiguationData":[OSD([sQuery(id+"F7.wireOp",EDGE,"E67")])],"isStart":false})]});
            var Q2;
            Q2=makeQuery(id+"F8.boolean.opBoolean","INTERSECT",EDGE,{"disambiguationData":[OD(1.0)],"derivedFrom":[makeQuery(id+"F5.opExtrude","SWEPT_FACE",FACE,{"disambiguationData":[OSD([sQuery(id+"F4.wireOp",EDGE,"E30")])]}),makeQuery(id+"F8.opExtrude","SWEPT_FACE",FACE,{"disambiguationData":[OSD([sQuery(id+"F7.wireOp",EDGE,"E67")])]})]});
            var Q3;
            {var subQ0=sQuery(id+"F4.wireOp",EDGE,"E30");Q3=makeQuery(id+"F8.boolean.opBoolean","SPLIT",EDGE,{"disambiguationData":[TD([makeQuery(id+"F5.opExtrude","SWEPT_FACE",FACE,{"disambiguationData":[OSD([sQuery(id+"F4.wireOp",EDGE,"E35.filletArc")])]})])],"derivedFrom":makeQuery(id+"F5.opExtrude","CAP_EDGE",EDGE,{"disambiguationData":[OSD([subQ0])],"isStart":false})});}
            var Q4;
            {var subQ0=sQuery(id+"F0.wireOp",EDGE,"E25.7");var subQ1=sQuery(id+"F0.wireOp",EDGE,"E25.1");var subQ2=sQuery(id+"F0.wireOp",EDGE,"E25.6");var subQ3=sQuery(id+"F0.wireOp",EDGE,"E25.5");var subQ4=sQuery(id+"F0.wireOp",EDGE,"E25.4");var subQ5=sQuery(id+"F0.wireOp",EDGE,"E25.0");var subQ6=sQuery(id+"F0.wireOp",EDGE,"E25.2");var subQ7=sQuery(id+"F0.wireOp",EDGE,"E25.3");Q4=makeQuery(id+"F8.boolean.opBoolean","INTERSECT",EDGE,{"derivedFrom":[makeQuery(id+"F5.boolean.opBoolean","SPLIT",FACE,{"disambiguationData":[TD([makeQuery(id+"F2.opExtrude","SWEPT_FACE",FACE,{"disambiguationData":[OSD([subQ5])]})])],"derivedFrom":makeQuery(id+"F3.boolean.opBoolean","COPY",FACE,{"derivedFrom":makeQuery(id+"F3.opExtrude","CAP_FACE",FACE,{"disambiguationData":[OSD([subQ5,subQ1,subQ6,subQ7,subQ4,subQ3,subQ2,subQ0])],"isStart":false})})}),makeQuery(id+"F8.opExtrude","SWEPT_FACE",FACE,{"disambiguationData":[OSD([sQuery(id+"F7.wireOp",EDGE,"E67")])]})]});}
            var Q5;
            Q5=makeQuery(id+"F8.boolean.opBoolean","INTERSECT",EDGE,{"disambiguationData":[OD(0.0)],"derivedFrom":[makeQuery(id+"F5.opExtrude","SWEPT_FACE",FACE,{"disambiguationData":[OSD([sQuery(id+"F4.wireOp",EDGE,"E30")])]}),makeQuery(id+"F8.opExtrude","SWEPT_FACE",FACE,{"disambiguationData":[OSD([sQuery(id+"F7.wireOp",EDGE,"E67")])]})]});
            fillet(context, id + "F14", {"entities" : qUnion([Q0, Q1, Q2, Q3, Q4, Q5]), "radius" : 3 * mm, "tangentPropagation" : true, "allowEdgeOverflow" : false});
        }
        {
            var Q0;
            Q0=makeQuery(id+"F1.opExtrude","CAP_EDGE",EDGE,{"disambiguationData":[OSD([sQuery(id+"F0.wireOp",EDGE,"E1.bottom")])],"isStart":false});
            fillet(context, id + "F15", {"entities" : qUnion([Q0]), "radius" : 2 * mm, "tangentPropagation" : true, "allowEdgeOverflow" : false});
        }
        {
            var Q0;
            {var subQ0=sQuery(id+"F0.wireOp",EDGE,"E21.filletArc");var subQ1=sQuery(id+"F0.wireOp",EDGE,"E7");var subQ2=sQuery(id+"F0.wireOp",EDGE,"E6");var subQ3=sQuery(id+"F0.wireOp",EDGE,"E5");var subQ4=sQuery(id+"F0.wireOp",EDGE,"E4");var subQ5=sQuery(id+"F0.wireOp",EDGE,"E22.filletArc");var subQ6=sQuery(id+"F0.wireOp",EDGE,"E1.bottom");var subQ7=sQuery(id+"F0.wireOp",EDGE,"E1.right");var subQ8=sQuery(id+"F0.wireOp",EDGE,"E1.top");var subQ9=sQuery(id+"F0.wireOp",EDGE,"E1.left");var subQ10=sQuery(id+"F0.wireOp",EDGE,"E23.filletArc");var subQ11=sQuery(id+"F0.wireOp",EDGE,"E24.filletArc");Q0=makeQuery(id+"F2.boolean.opBoolean","SPLIT",FACE,{"disambiguationData":[TD([makeQuery(id+"F1.opExtrude","SWEPT_FACE",FACE,{"disambiguationData":[OSD([subQ6])]})])],"derivedFrom":makeQuery(id+"F1.opExtrude","CAP_FACE",FACE,{"disambiguationData":[OSD([subQ6,subQ8,subQ9,subQ7,subQ4,subQ3,subQ2,subQ1,subQ0,subQ5,subQ10,subQ11])],"isStart":true})});}
            var sketch = newSketch(context, id + "F16", { "sketchPlane" : qUnion([Q0])});
            skCircle(sketch, "E79", {"center": v(0, 120) * mm, "radius": 6 * mm});
            skLineSegment(sketch, "E80", {"start": v(0, 120) * mm, "end": v(0, 90) * mm, "construction": true});
            skLineSegment(sketch, "E81", {"start": v(-33, 90) * mm, "end": v(-15, 108) * mm});
            skLineSegment(sketch, "E82", {"start": v(33, 90) * mm, "end": v(15, 108) * mm});
            skArc(sketch, "E83", {"start": v(15, 120) * mm, "mid": v(0, 135) * mm, "end": v(-15, 120) * mm});
            skLineSegment(sketch, "E84", {"start": v(-15, 120) * mm, "end": v(-15, 108) * mm});
            skLineSegment(sketch, "E85", {"start": v(15, 120) * mm, "end": v(15, 108) * mm});
            skLineSegment(sketch, "E86", {"start": v(-80, 0) * mm, "end": v(80, 0) * mm, "construction": true});
            skLineSegment(sketch, "E87.MirrorCS", {"start": v(0, -120) * mm, "end": v(0, -90) * mm, "construction": true});
            skLineSegment(sketch, "E88.MirrorCS", {"start": v(-33, -90) * mm, "end": v(-15, -108) * mm});
            skLineSegment(sketch, "E89.MirrorCS", {"start": v(33, -90) * mm, "end": v(15, -108) * mm});
            skArc(sketch, "E90.MirrorCS", {"start": v(15, -120) * mm, "mid": v(0, -135) * mm, "end": v(-15, -120) * mm});
            skLineSegment(sketch, "E91.MirrorCS", {"start": v(-15, -120) * mm, "end": v(-15, -108) * mm});
            skCircle(sketch, "E92.MirrorC", {"center": v(0, -120) * mm, "radius": 6 * mm});
            skLineSegment(sketch, "E93.MirrorCS", {"start": v(15, -120) * mm, "end": v(15, -108) * mm});
            skSolve(sketch);
        }
        {
            var Q0;
            Q0=makeQuery(id+"F16.imprint","IMPRINT",FACE,{"disambiguationData":[TD([[makeQuery(id+"F16.imprint","IMPRINT",EDGE,{"derivedFrom":sQuery(id+"F16.wireOp",EDGE,"E79")}),-1.0]])]});
            var Q1;
            {var subQ1=sQuery(id+"F16.wireOp",EDGE,"E88.MirrorCS");Q1=makeQuery(id+"F16.imprint","IMPRINT",FACE,{"disambiguationData":[TD([[makeQuery(id+"F16.imprint","IMPRINT",EDGE,{"derivedFrom":subQ1}),1.0]])]});}
            var Q2;
            Q2=makeQuery(id+"F16.imprint","IMPRINT",FACE,{"disambiguationData":[TD([[makeQuery(id+"F16.imprint","IMPRINT",EDGE,{"derivedFrom":makeQuery(id+"F1.opExtrude","CAP_EDGE",EDGE,{"disambiguationData":[OSD([sQuery(id+"F0.wireOp",EDGE,"E1.left")])],"isStart":true})}),-1.0]])]});
            var Q3;
            Q3=makeQuery(id+"F2.opExtrude","CAP_FACE",FACE,{"disambiguationData":[OSD([sQuery(id+"F0.wireOp",EDGE,"E12"),sQuery(id+"F0.wireOp",EDGE,"E13"),sQuery(id+"F0.wireOp",EDGE,"E14"),sQuery(id+"F0.wireOp",EDGE,"E15"),sQuery(id+"F0.wireOp",EDGE,"E17.filletArc"),sQuery(id+"F0.wireOp",EDGE,"E18.filletArc"),sQuery(id+"F0.wireOp",EDGE,"E19.filletArc"),sQuery(id+"F0.wireOp",EDGE,"E20.filletArc"),sQuery(id+"F0.wireOp",EDGE,"E25.0"),sQuery(id+"F0.wireOp",EDGE,"E25.1"),sQuery(id+"F0.wireOp",EDGE,"E25.2"),sQuery(id+"F0.wireOp",EDGE,"E25.3"),sQuery(id+"F0.wireOp",EDGE,"E25.4"),sQuery(id+"F0.wireOp",EDGE,"E25.5"),sQuery(id+"F0.wireOp",EDGE,"E25.6"),sQuery(id+"F0.wireOp",EDGE,"E25.7")])],"isStart":false});
            extrude(context, id + "F17", {"entities" : qUnion([Q0, Q1, Q2]), "endBound" : BoundingType.UP_TO_SURFACE, "endBoundEntityFace" : qUnion([Q3]), "depth" : 25 * mm});
        }
    });
